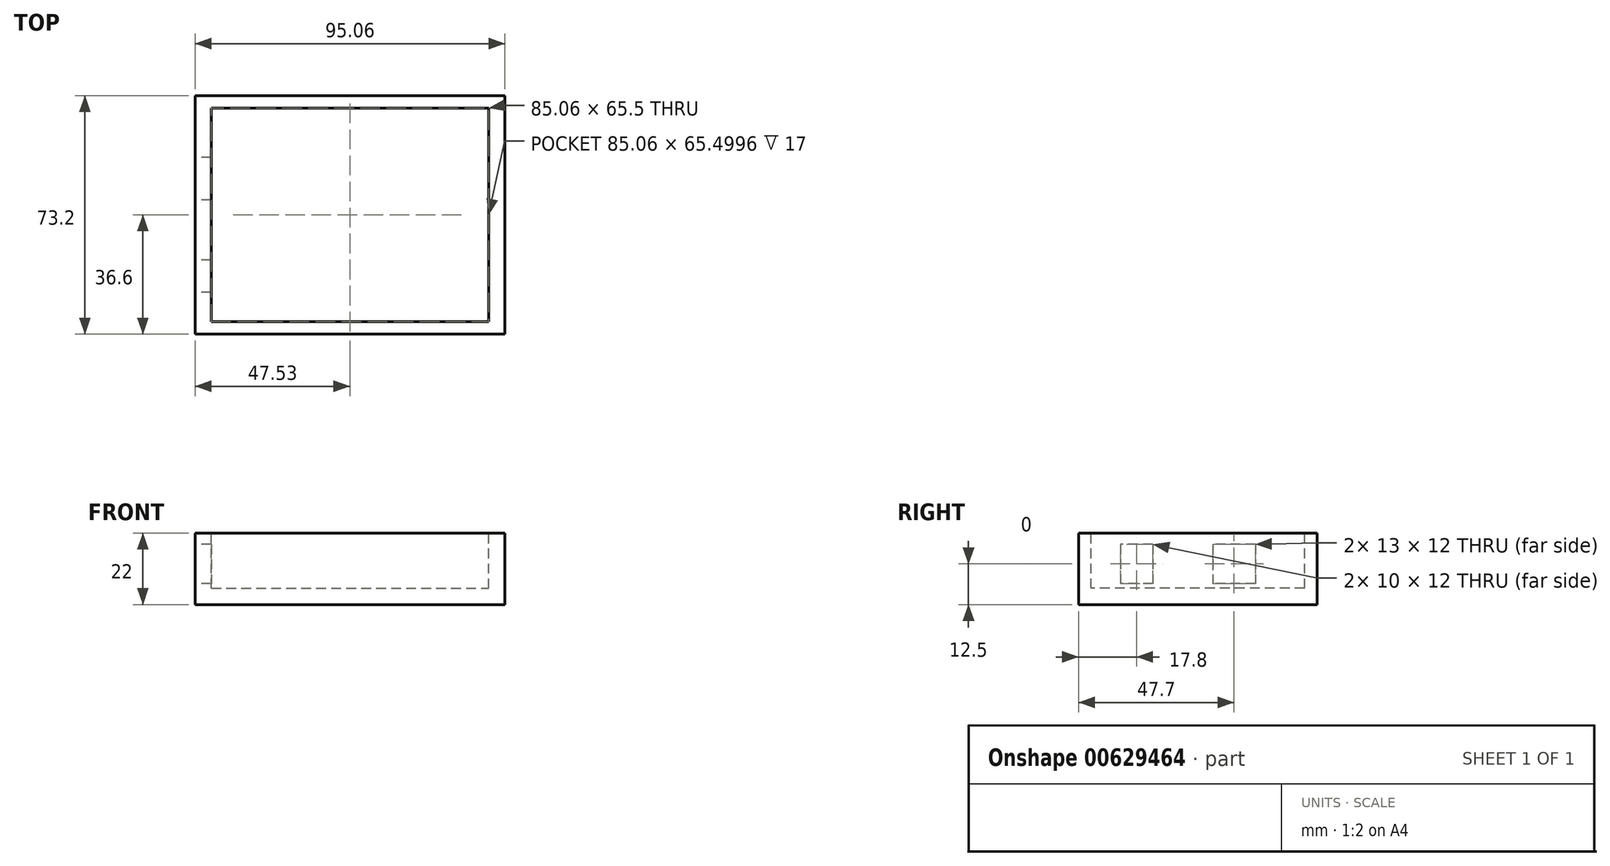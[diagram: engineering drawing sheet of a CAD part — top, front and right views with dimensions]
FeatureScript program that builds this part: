
annotation { "Feature Type Name" : "Feature", "Feature Type Description" : "" }
export const myFeature = defineFeature(function(context is Context, id is Id, definition is map)
    precondition{}
    {
        {
            assignVariable(context, id + "F0", {"name" : "boxHeightMin", "anyValue" : 12});
        }
        {
            var Q0;
            Q0=qCreatedBy(makeId("Top.planeOp"),FACE);
            var sketch = newSketch(context, id + "F1", { "sketchPlane" : qUnion([Q0])});
            skLineSegment(sketch, "E0.bottom", {"start": v(-53.8, 24.27) * mm, "end": v(41.26, 24.27) * mm});
            skLineSegment(sketch, "E0.top", {"start": v(-53.8, -48.93) * mm, "end": v(41.26, -48.93) * mm});
            skLineSegment(sketch, "E0.left", {"start": v(-53.8, 24.27) * mm, "end": v(-53.8, -48.93) * mm});
            skLineSegment(sketch, "E0.right", {"start": v(41.26, 24.27) * mm, "end": v(41.26, -48.93) * mm});
            skSolve(sketch);
        }
        {
            var Q0;
            Q0=makeQuery(id+"F1.imprint","IMPRINT",FACE,{"disambiguationData":[TD([[makeQuery(id+"F1.imprint","IMPRINT",EDGE,{"derivedFrom":sQuery(id+"F1.wireOp",EDGE,"E0.bottom")}),-1.0]])]});
            extrude(context, id + "F2", {"entities" : qUnion([Q0]), "depth" : (getVariable(context, 'boxHeightMin') + 10) * mm, "offsetDistance" : 25 * mm});
        }
        {
            var Q0;
            Q0=makeQuery(id+"F2.opExtrude","CAP_FACE",FACE,{"disambiguationData":[OSD([sQuery(id+"F1.wireOp",EDGE,"E0.bottom"),sQuery(id+"F1.wireOp",EDGE,"E0.top"),sQuery(id+"F1.wireOp",EDGE,"E0.left"),sQuery(id+"F1.wireOp",EDGE,"E0.right")])],"isStart":false});
            var sketch = newSketch(context, id + "F3", { "sketchPlane" : qUnion([Q0])});
            skLineSegment(sketch, "E1", {"start": v(-53.8, 24.27) * mm, "end": v(41.26, -48.93) * mm, "construction": true});
            skLineSegment(sketch, "E2", {"start": v(-53.8, -48.93) * mm, "end": v(41.26, 24.27) * mm, "construction": true});
            skLineSegment(sketch, "E3.bottom", {"start": v(-48.8, 20.42) * mm, "end": v(36.26, 20.42) * mm});
            skLineSegment(sketch, "E3.top", {"start": v(-48.8, -45.08) * mm, "end": v(36.26, -45.08) * mm});
            skLineSegment(sketch, "E3.left", {"start": v(-48.8, 20.42) * mm, "end": v(-48.8, -45.08) * mm});
            skLineSegment(sketch, "E3.right", {"start": v(36.26, 20.42) * mm, "end": v(36.26, -45.08) * mm});
            skSolve(sketch);
        }
        {
            var Q0;
            Q0=makeQuery(id+"F3.imprint","IMPRINT",FACE,{"disambiguationData":[TD([[makeQuery(id+"F3.imprint","IMPRINT",EDGE,{"derivedFrom":sQuery(id+"F3.wireOp",EDGE,"E3.bottom")}),-1.0]])]});
            extrude(context, id + "F4", {"entities" : qUnion([Q0]), "operationType" : NewBodyOperationType.REMOVE, "oppositeDirection" : true, "depth" : (getVariable(context, 'boxHeightMin') + 5) * mm, "offsetDistance" : 25 * mm});
        }
        {
            var Q0;
            Q0=makeQuery(id+"F2.opExtrude","SWEPT_FACE",FACE,{"disambiguationData":[OSD([sQuery(id+"F1.wireOp",EDGE,"E0.left")])]});
            var sketch = newSketch(context, id + "F5", { "sketchPlane" : qUnion([Q0])});
            skLineSegment(sketch, "E4.bottom", {"start": v(-5.27, 18.5) * mm, "end": v(7.73, 18.5) * mm});
            skLineSegment(sketch, "E4.top", {"start": v(-5.27, 6.5) * mm, "end": v(7.73, 6.5) * mm});
            skLineSegment(sketch, "E4.left", {"start": v(-5.27, 18.5) * mm, "end": v(-5.27, 6.5) * mm});
            skLineSegment(sketch, "E4.right", {"start": v(7.73, 18.5) * mm, "end": v(7.73, 6.5) * mm});
            skLineSegment(sketch, "E5.bottom", {"start": v(26.13, 18.5) * mm, "end": v(36.13, 18.5) * mm});
            skLineSegment(sketch, "E5.top", {"start": v(26.13, 6.5) * mm, "end": v(36.13, 6.5) * mm});
            skLineSegment(sketch, "E5.left", {"start": v(26.13, 18.5) * mm, "end": v(26.13, 6.5) * mm});
            skLineSegment(sketch, "E5.right", {"start": v(36.13, 18.5) * mm, "end": v(36.13, 6.5) * mm});
            skSolve(sketch);
        }
        {
            var Q0;
            Q0=makeQuery(id+"F5.imprint","IMPRINT",FACE,{"disambiguationData":[TD([[makeQuery(id+"F5.imprint","IMPRINT",EDGE,{"derivedFrom":sQuery(id+"F5.wireOp",EDGE,"E4.bottom")}),-1.0]])]});
            extrude(context, id + "F6", {"entities" : qUnion([Q0]), "operationType" : NewBodyOperationType.REMOVE, "oppositeDirection" : true, "depth" : 5 * mm, "offsetDistance" : 25 * mm});
        }
        {
            var Q0;
            Q0=makeQuery(id+"F5.imprint","IMPRINT",FACE,{"disambiguationData":[TD([[makeQuery(id+"F5.imprint","IMPRINT",EDGE,{"derivedFrom":sQuery(id+"F5.wireOp",EDGE,"E5.bottom")}),-1.0]])]});
            extrude(context, id + "F7", {"entities" : qUnion([Q0]), "operationType" : NewBodyOperationType.REMOVE, "oppositeDirection" : true, "depth" : 5 * mm, "offsetDistance" : 25 * mm});
        }
    });
